# Revit family: H-201_RFA
name_source: partatom
category: Aparatos sanitarios
units: mm (PartAtom-declared; Revit-internal decimal feet)

## family parameters
Activar corte en vistas = No
Compartido = No
Corte con vacíos al cargar = No
Cota de conector redondo = Usar diámetro
Mantener orientación de anotación = No
Número OmniClass = 23.45.00.00
Punto de cálculo de habitación = No
Se basa en plano de trabajo = No
Siempre vertical = Sí
Tipo de pieza = Normal
Título OmniClass = Sanitary, Laundry, and Cleaning Equipment

## types (1)
- H-201
    Brass Chromed = Brass
    Comentarios de tipo = Showerheads
    Compliance = NOM-008-CONAGUA-1998
    Descripción = Regadera de Baja, Media y Alta Presión Economizador Dinámico de Agua Cumple con la Norma NOM-008-CONAGUA-1998 Con Sistema Anticalcáreo Incluye Nudo Móvil
    Elevación por defecto = 75"
    Fabricante = HELVEX
    Features = Regadera de Baja, Media y Alta Presión Economizador Dinámico de Agua Cumple con la Norma NOM-008-CONAGUA-1998 Con Sistema Anticalcáreo Incluye Nudo Móvil
    Imagen de tipo = H-201.jpg
    Inlet Threads = ½" - 14 NPT
    Max. Water Flow = 2.6 gal/min
    Max. Working Pressure = 85.3 psi
    Min. Water Flow = 1.1 gal/min
    Min. Working Pressure = 2.8 psi
    Modelo = H-201
    Total Length = 7"
    Total Width = 4"
    URL = https://helvex.com.mx

## geometry (parser evidence)
native form markers: Sweep x3
no freeform markers — native parametric forms only
